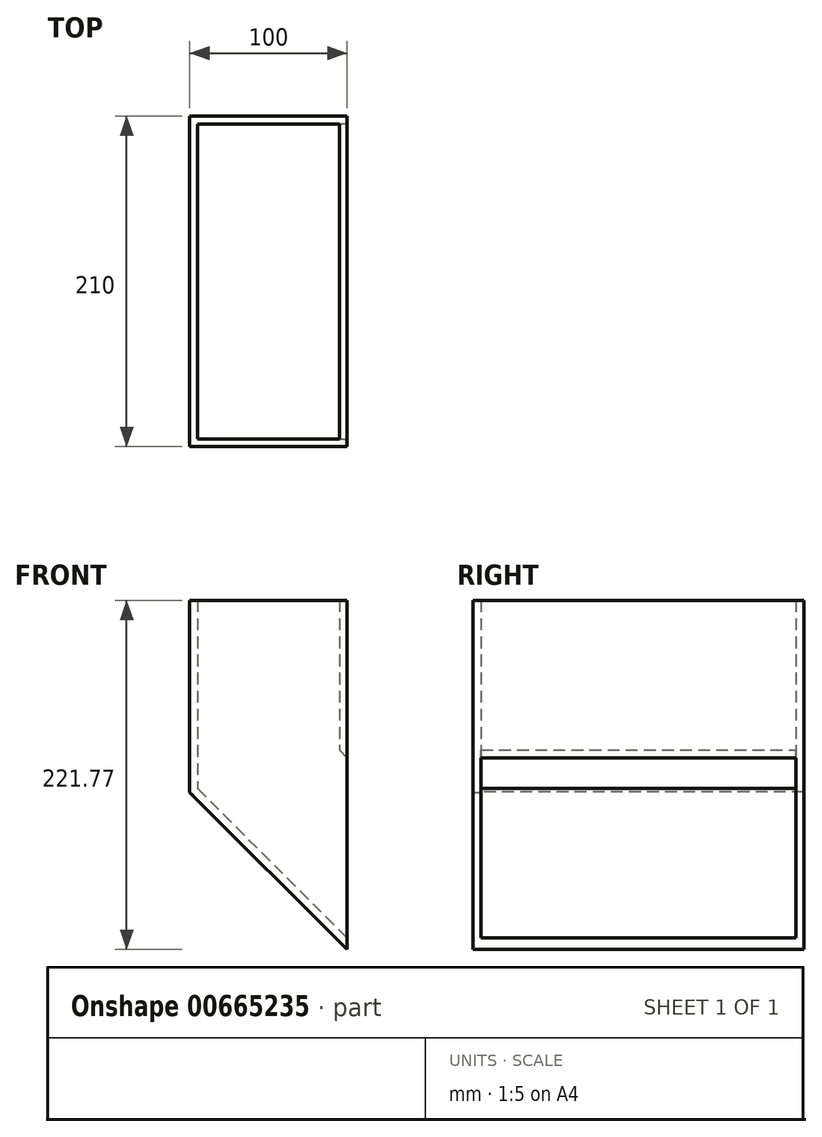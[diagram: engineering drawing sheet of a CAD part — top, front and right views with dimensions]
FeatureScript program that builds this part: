
annotation { "Feature Type Name" : "Feature", "Feature Type Description" : "" }
export const myFeature = defineFeature(function(context is Context, id is Id, definition is map)
    precondition{}
    {
        {
            var Q0;
            Q0=qCreatedBy(makeId("Front.planeOp"),FACE);
            var sketch = newSketch(context, id + "F0", { "sketchPlane" : qUnion([Q0])});
            skLineSegment(sketch, "E0", {"start": v(0, 0) * mm, "end": v(-200, 0) * mm, "construction": true});
            skLineSegment(sketch, "E1", {"start": v(0, 0) * mm, "end": v(-60.81, -60.81) * mm, "construction": true});
            skLineSegment(sketch, "E2", {"start": v(-100, 0) * mm, "end": v(-100, -77.94) * mm});
            skLineSegment(sketch, "E3", {"start": v(-60.81, -60.81) * mm, "end": v(-100, -21.62) * mm, "construction": true});
            skLineSegment(sketch, "E4", {"start": v(-100, 0) * mm, "end": v(-100, 200) * mm});
            skLineSegment(sketch, "E5", {"start": v(0, 0) * mm, "end": v(-100, 100) * mm, "construction": true});
            skLineSegment(sketch, "E6", {"start": v(-100, 107.07) * mm, "end": v(0, 7.07) * mm, "construction": true});
            skLineSegment(sketch, "E7", {"start": v(-100, -21.62) * mm, "end": v(-200, 78.38) * mm});
            skLineSegment(sketch, "E8", {"start": v(0, 0) * mm, "end": v(0, 200) * mm, "construction": true});
            skLineSegment(sketch, "E9", {"start": v(0, 200) * mm, "end": v(-200, 200) * mm});
            skLineSegment(sketch, "E10", {"start": v(-200, 78.38) * mm, "end": v(-200, 200) * mm});
            skLineSegment(sketch, "E11", {"start": v(-195, 200) * mm, "end": v(-195, 80.45) * mm});
            skLineSegment(sketch, "E12", {"start": v(-195, 80.45) * mm, "end": v(-100, -14.55) * mm});
            skLineSegment(sketch, "E13", {"start": v(-105, 200) * mm, "end": v(-105, 105) * mm});
            skLineSegment(sketch, "E14", {"start": v(-100, 100) * mm, "end": v(-105, 105) * mm});
            skSolve(sketch);
        }
        {
            var Q0;
            Q0=qSketchRegion(id+"F0",true);
            extrude(context, id + "F1", {"entities" : qUnion([Q0]), "oppositeDirection" : true, "depth" : 5 * mm});
        }
        {
            var Q0;
            {var subQ3=sQuery(id+"F0.wireOp",EDGE,"E7");Q0=makeQuery(id+"F0.imprint","IMPRINT",FACE,{"disambiguationData":[TD([[makeQuery(id+"F0.imprint","IMPRINT",EDGE,{"derivedFrom":subQ3}),-1.0]])]});}
            var Q1;
            {var subQ4=sQuery(id+"F0.wireOp",EDGE,"E13");Q1=makeQuery(id+"F0.imprint","IMPRINT",FACE,{"disambiguationData":[TD([[makeQuery(id+"F0.imprint","IMPRINT",EDGE,{"derivedFrom":subQ4}),1.0]])]});}
            extrude(context, id + "F2", {"entities" : qUnion([Q0, Q1]), "operationType" : NewBodyOperationType.ADD, "depth" : 200 * mm});
        }
        {
            var Q0;
            {var subQ0=sQuery(id+"F0.wireOp",EDGE,"E11");Q0=makeQuery(id+"F0.imprint","IMPRINT",FACE,{"disambiguationData":[TD([[makeQuery(id+"F0.imprint","IMPRINT",EDGE,{"derivedFrom":subQ0}),1.0]])]});}
            cPlane(context, id + "F3", {"entities" : qUnion([Q0]), "cplaneType" : CPlaneType.OFFSET, "offset" : 200 * mm, "width" : 150 * mm, "height" : 150 * mm});
        }
        {
            var Q0;
            Q0=qCreatedBy(id+"F3.planeOp",FACE);
            var sketch = newSketch(context, id + "F4", { "sketchPlane" : qUnion([Q0])});
            skLineSegment(sketch, "E15", {"start": v(0, 0) * mm, "end": v(0, 200) * mm, "construction": true});
            skLineSegment(sketch, "E16", {"start": v(0, 200) * mm, "end": v(-200, 200) * mm});
            skLineSegment(sketch, "E17", {"start": v(-200, 200) * mm, "end": v(-200, 77.86) * mm});
            skLineSegment(sketch, "E18", {"start": v(0, 0) * mm, "end": v(-60.81, -60.81) * mm});
            skLineSegment(sketch, "E19", {"start": v(-60.81, -60.81) * mm, "end": v(-200, 77.86) * mm});
            skLineSegment(sketch, "E20", {"start": v(-100, 200) * mm, "end": v(-100, -21.77) * mm});
            skPoint(sketch, "E20.endSnap0", {"position": v(-100, 200) * mm});
            skSolve(sketch);
        }
        {
            var Q0;
            Q0=qSketchRegion(id+"F4",true);
            extrude(context, id + "F5", {"entities" : qUnion([Q0]), "operationType" : NewBodyOperationType.ADD, "depth" : 5 * mm});
        }
    });
